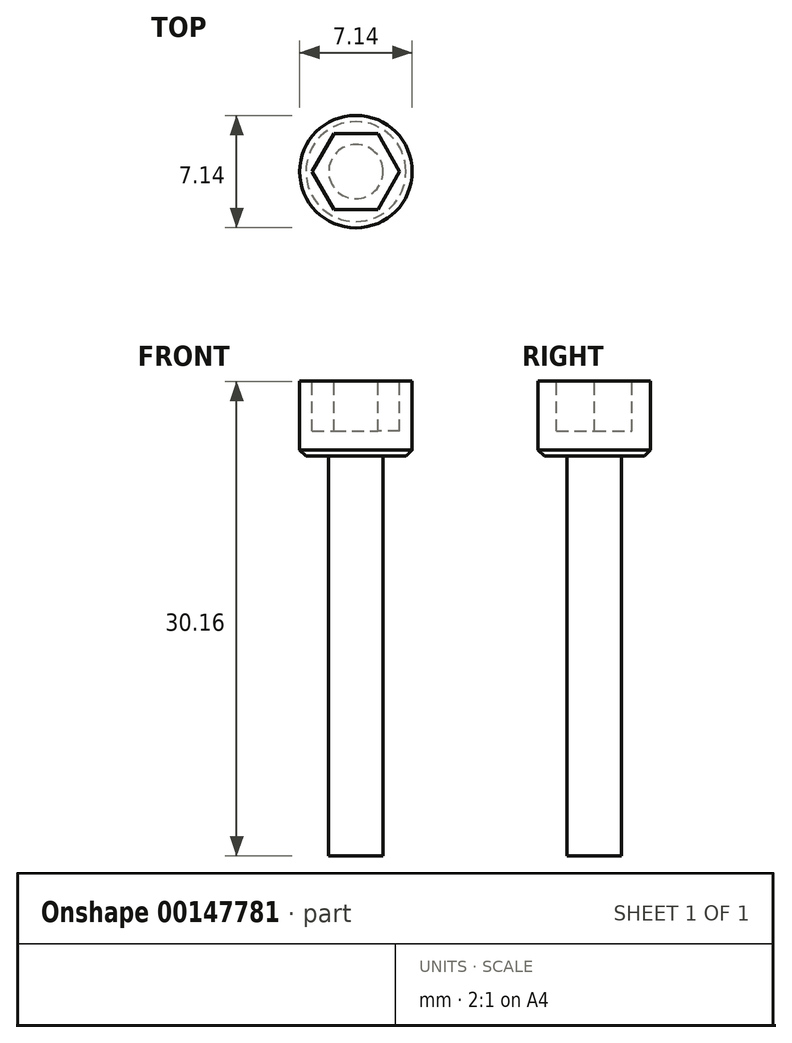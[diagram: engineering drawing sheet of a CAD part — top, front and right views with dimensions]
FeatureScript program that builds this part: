
annotation { "Feature Type Name" : "Feature", "Feature Type Description" : "" }
export const myFeature = defineFeature(function(context is Context, id is Id, definition is map)
    precondition{}
    {
        {
            var Q0;
            Q0=qCreatedBy(makeId("Top.planeOp"),FACE);
            var sketch = newSketch(context, id + "F0", { "sketchPlane" : qUnion([Q0])});
            skCircle(sketch, "E0", {"center": v(0, 0) * mm, "radius": 1.73 * mm});
            skSolve(sketch);
        }
        {
            var Q0;
            Q0=qSketchRegion(id+"F0",true);
            extrude(context, id + "F1", {"entities" : qUnion([Q0]), "depth" : 25.4 * mm});
        }
        {
            var Q0;
            Q0=makeQuery(id+"F1.opExtrude","CAP_FACE",FACE,{"disambiguationData":[OSD([sQuery(id+"F0.wireOp",EDGE,"E0")])],"isStart":false});
            var sketch = newSketch(context, id + "F2", { "sketchPlane" : qUnion([Q0])});
            skCircle(sketch, "E1", {"center": v(0, 0) * mm, "radius": 3.57 * mm});
            skSolve(sketch);
        }
        {
            var Q0;
            Q0=qSketchRegion(id+"F2",true);
            extrude(context, id + "F3", {"entities" : qUnion([Q0]), "operationType" : NewBodyOperationType.ADD, "depth" : 4.76 * mm});
        }
        {
            var Q0;
            Q0=makeQuery(id+"F3.opExtrude","CAP_FACE",FACE,{"disambiguationData":[OSD([sQuery(id+"F2.wireOp",EDGE,"E1")])],"isStart":false});
            var sketch = newSketch(context, id + "F4", { "sketchPlane" : qUnion([Q0])});
            skCircle(sketch, "E2.cCircle", {"center": v(0, 0) * mm, "radius": 2.4 * mm, "construction": true});
            skLineSegment(sketch, "E2.0", {"start": v(-1.39, 2.4) * mm, "end": v(1.39, 2.4) * mm});
            skLineSegment(sketch, "E2.1", {"start": v(1.39, 2.4) * mm, "end": v(2.78, 0) * mm});
            skLineSegment(sketch, "E2.2", {"start": v(2.78, 0) * mm, "end": v(1.39, -2.4) * mm});
            skLineSegment(sketch, "E2.3", {"start": v(1.39, -2.4) * mm, "end": v(-1.39, -2.4) * mm});
            skLineSegment(sketch, "E2.4", {"start": v(-1.39, -2.4) * mm, "end": v(-2.78, 0) * mm});
            skLineSegment(sketch, "E2.5", {"start": v(-2.78, 0) * mm, "end": v(-1.39, 2.4) * mm});
            skPoint(sketch, "E2.0.midPoint", {"position": v(0, 2.4) * mm});
            skSolve(sketch);
        }
        {
            var Q0;
            Q0=qSketchRegion(id+"F4",true);
            extrude(context, id + "F5", {"entities" : qUnion([Q0]), "operationType" : NewBodyOperationType.REMOVE, "oppositeDirection" : true, "depth" : 3.17 * mm});
        }
        {
            var Q0;
            Q0=makeQuery(id+"F3.opExtrude","CAP_EDGE",EDGE,{"disambiguationData":[OSD([sQuery(id+"F2.wireOp",EDGE,"E1")])],"isStart":true});
            chamfer(context, id + "F6", {"entities" : qUnion([Q0]), "width" : 0.4 * mm, "tangentPropagation" : true});
        }
    });
